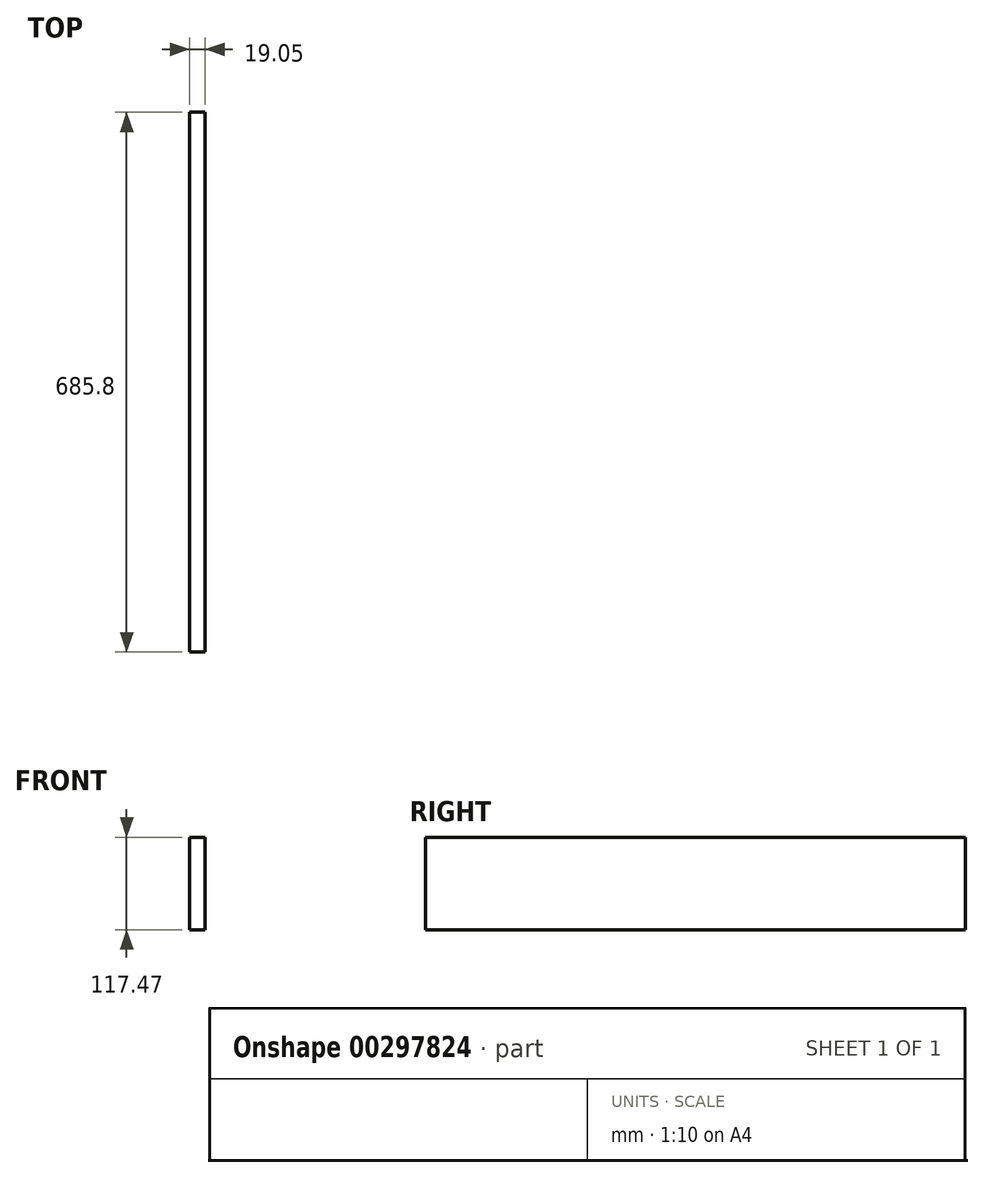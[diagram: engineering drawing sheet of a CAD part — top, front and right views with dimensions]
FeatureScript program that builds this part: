
annotation { "Feature Type Name" : "Feature", "Feature Type Description" : "" }
export const myFeature = defineFeature(function(context is Context, id is Id, definition is map)
    precondition{}
    {
        {
            var Q0;
            Q0=qCreatedBy(makeId("Right.planeOp"),FACE);
            var sketch = newSketch(context, id + "F0", { "sketchPlane" : qUnion([Q0])});
            skLineSegment(sketch, "E0.bottom", {"start": v(3.3, 0) * mm, "end": v(689.1, 0) * mm});
            skLineSegment(sketch, "E0.top", {"start": v(3.3, 117.48) * mm, "end": v(689.1, 117.48) * mm});
            skLineSegment(sketch, "E0.left", {"start": v(3.3, 0) * mm, "end": v(3.3, 117.48) * mm});
            skLineSegment(sketch, "E0.right", {"start": v(689.1, 0) * mm, "end": v(689.1, 117.48) * mm});
            skSolve(sketch);
        }
        {
            var Q0;
            Q0=makeQuery(id+"F0.imprint","IMPRINT",FACE,{"disambiguationData":[TD([[makeQuery(id+"F0.imprint","IMPRINT",EDGE,{"derivedFrom":sQuery(id+"F0.wireOp",EDGE,"E0.bottom")}),1.0]])]});
            extrude(context, id + "F1", {"entities" : qUnion([Q0]), "depth" : 19.05 * mm});
        }
    });
